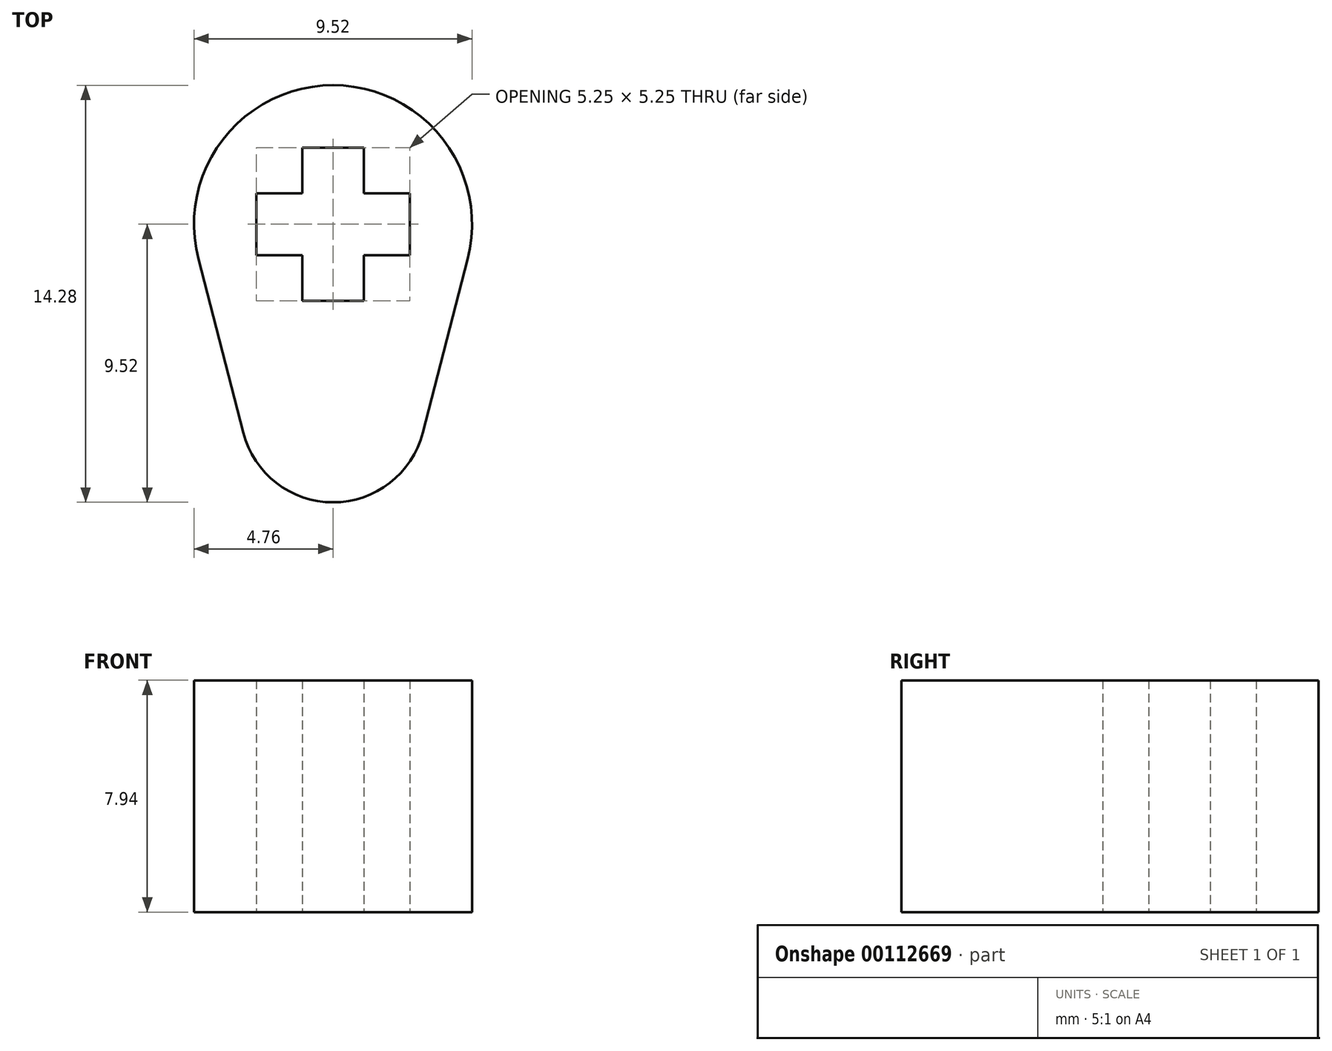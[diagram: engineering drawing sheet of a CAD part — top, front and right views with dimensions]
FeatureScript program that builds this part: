
annotation { "Feature Type Name" : "Feature", "Feature Type Description" : "" }
export const myFeature = defineFeature(function(context is Context, id is Id, definition is map)
    precondition{}
    {
        {
            var Q0;
            Q0=qCreatedBy(makeId("Top.planeOp"),FACE);
            var sketch = newSketch(context, id + "F0", { "sketchPlane" : qUnion([Q0])});
            skLineSegment(sketch, "E0.bottom", {"start": v(1.06, 2.63) * mm, "end": v(-1.06, 2.63) * mm});
            skLineSegment(sketch, "E0.top", {"start": v(1.06, -2.63) * mm, "end": v(-1.06, -2.63) * mm});
            skLineSegment(sketch, "E0.left", {"start": v(1.06, 2.63) * mm, "end": v(1.06, -2.63) * mm});
            skLineSegment(sketch, "E0.right", {"start": v(-1.06, 2.63) * mm, "end": v(-1.06, -2.63) * mm});
            skPoint(sketch, "E0.middle", {"position": v(0, 0) * mm});
            skLineSegment(sketch, "E1.bottom", {"start": v(2.63, -1.06) * mm, "end": v(-2.63, -1.06) * mm});
            skLineSegment(sketch, "E1.top", {"start": v(2.63, 1.06) * mm, "end": v(-2.63, 1.06) * mm});
            skLineSegment(sketch, "E1.left", {"start": v(2.63, -1.06) * mm, "end": v(2.63, 1.06) * mm});
            skLineSegment(sketch, "E1.right", {"start": v(-2.63, -1.06) * mm, "end": v(-2.63, 1.06) * mm});
            skArc(sketch, "E2", {"start": v(4.61, -1.2) * mm, "mid": v(0, 4.76) * mm, "end": v(-4.61, -1.2) * mm});
            skLineSegment(sketch, "E3", {"start": v(-4.61, -1.2) * mm, "end": v(-3.07, -7.14) * mm});
            skLineSegment(sketch, "E4", {"start": v(4.61, -1.2) * mm, "end": v(3.07, -7.14) * mm});
            skLineSegment(sketch, "E5", {"start": v(0, 0) * mm, "end": v(0, -6.35) * mm, "construction": true});
            skArc(sketch, "E6", {"start": v(-3.07, -7.14) * mm, "mid": v(0, -9.53) * mm, "end": v(3.07, -7.14) * mm});
            skSolve(sketch);
        }
        {
            var Q0;
            Q0 = qSketchRegion(id + "F0", true);
            extrude(context, id + "F1", {"entities" : qUnion([Q0]), "depth" : 7.94 * mm});
        }
    });
